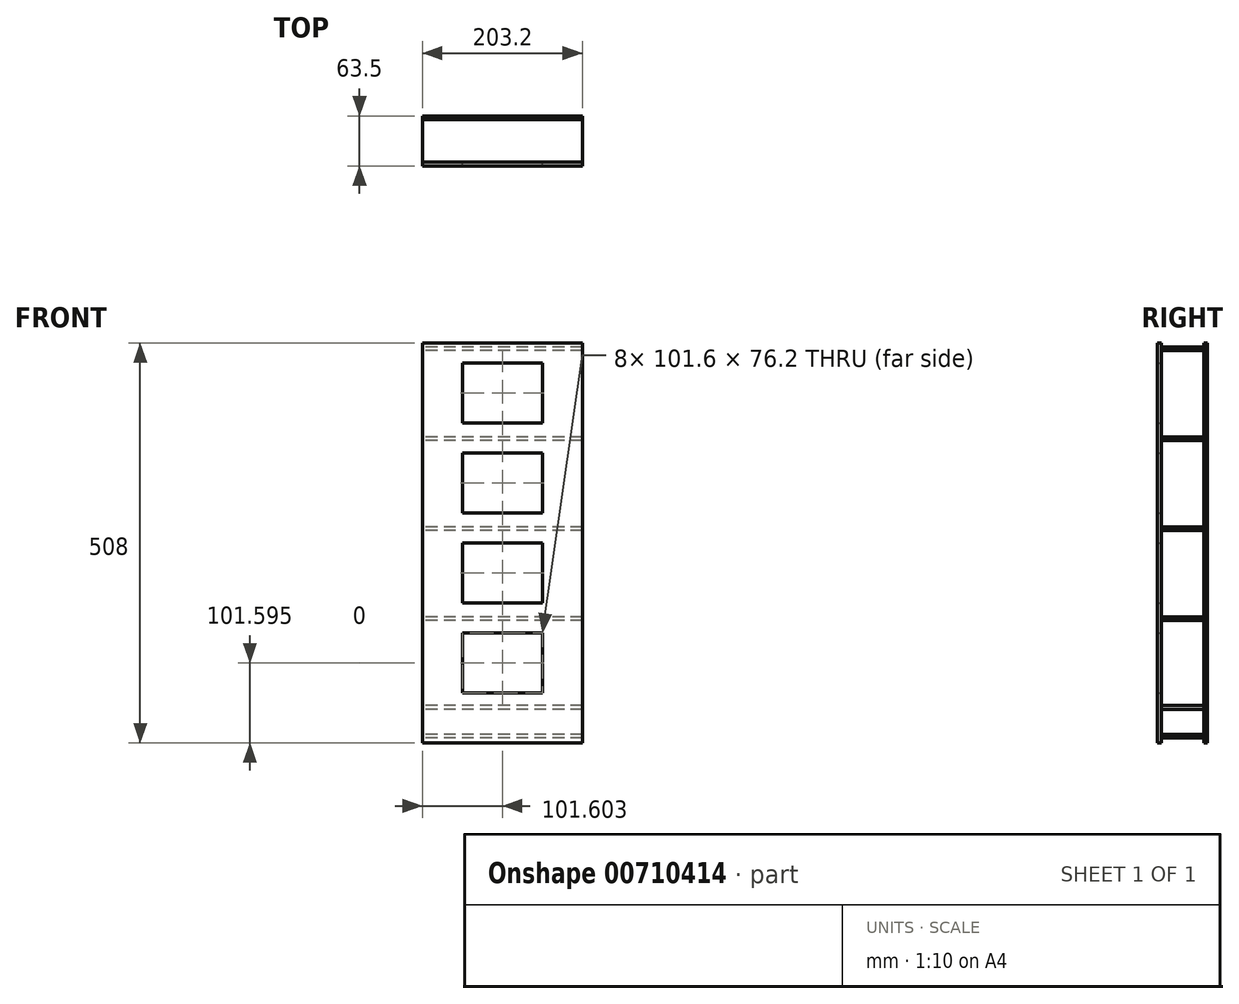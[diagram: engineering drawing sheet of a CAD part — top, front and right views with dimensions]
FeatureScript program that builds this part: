
annotation { "Feature Type Name" : "Feature", "Feature Type Description" : "" }
export const myFeature = defineFeature(function(context is Context, id is Id, definition is map)
    precondition{}
    {
        {
            var Q0;
            Q0=qCreatedBy(makeId("Front.planeOp"),FACE);
            var sketch = newSketch(context, id + "F0", { "sketchPlane" : qUnion([Q0])});
            skLineSegment(sketch, "E0.bottom", {"start": v(-77.18, 365.59) * mm, "end": v(126.02, 365.59) * mm});
            skLineSegment(sketch, "E0.top", {"start": v(-77.18, -142.41) * mm, "end": v(126.02, -142.41) * mm});
            skLineSegment(sketch, "E0.left", {"start": v(-77.18, 365.59) * mm, "end": v(-77.18, -142.41) * mm});
            skLineSegment(sketch, "E0.right", {"start": v(126.02, 365.59) * mm, "end": v(126.02, -142.41) * mm});
            skLineSegment(sketch, "E1.bottom", {"start": v(-26.38, 340.19) * mm, "end": v(75.22, 340.19) * mm});
            skLineSegment(sketch, "E1.top", {"start": v(-26.38, 263.99) * mm, "end": v(75.22, 263.99) * mm});
            skLineSegment(sketch, "E1.left", {"start": v(-26.38, 340.19) * mm, "end": v(-26.38, 263.99) * mm});
            skLineSegment(sketch, "E1.right", {"start": v(75.22, 340.19) * mm, "end": v(75.22, 263.99) * mm});
            skLineSegment(sketch, "E2.bottom", {"start": v(-26.38, 225.89) * mm, "end": v(75.22, 225.89) * mm});
            skLineSegment(sketch, "E2.top", {"start": v(-26.38, 149.69) * mm, "end": v(75.22, 149.69) * mm});
            skLineSegment(sketch, "E2.left", {"start": v(-26.38, 225.89) * mm, "end": v(-26.38, 149.69) * mm});
            skLineSegment(sketch, "E2.right", {"start": v(75.22, 225.89) * mm, "end": v(75.22, 149.69) * mm});
            skLineSegment(sketch, "E3.bottom", {"start": v(-26.38, 111.59) * mm, "end": v(75.22, 111.59) * mm});
            skLineSegment(sketch, "E3.top", {"start": v(-26.38, 35.39) * mm, "end": v(75.22, 35.39) * mm});
            skLineSegment(sketch, "E3.left", {"start": v(-26.38, 111.59) * mm, "end": v(-26.38, 35.39) * mm});
            skLineSegment(sketch, "E3.right", {"start": v(75.22, 111.59) * mm, "end": v(75.22, 35.39) * mm});
            skLineSegment(sketch, "E4.bottom", {"start": v(-26.38, -2.71) * mm, "end": v(75.22, -2.71) * mm});
            skLineSegment(sketch, "E4.top", {"start": v(-26.38, -78.91) * mm, "end": v(75.22, -78.91) * mm});
            skLineSegment(sketch, "E4.left", {"start": v(-26.38, -2.71) * mm, "end": v(-26.38, -78.91) * mm});
            skLineSegment(sketch, "E4.right", {"start": v(75.22, -2.71) * mm, "end": v(75.22, -78.91) * mm});
            skSolve(sketch);
        }
        {
            var Q0;
            Q0=makeQuery(id+"F0.imprint","IMPRINT",FACE,{"disambiguationData":[TD([[makeQuery(id+"F0.imprint","IMPRINT",EDGE,{"derivedFrom":sQuery(id+"F0.wireOp",EDGE,"E0.bottom")}),-1.0]])]});
            extrude(context, id + "F1", {"entities" : qUnion([Q0]), "depth" : 63.5 * mm, "offsetDistance" : 25.4 * mm});
        }
        {
            var Q0;
            Q0=makeQuery(id+"F1.opExtrude","SWEPT_FACE",FACE,{"disambiguationData":[OSD([sQuery(id+"F0.wireOp",EDGE,"E0.right")])]});
            var sketch = newSketch(context, id + "F2", { "sketchPlane" : qUnion([Q0])});
            skLineSegment(sketch, "E5.bottom", {"start": v(-58.74, 365.59) * mm, "end": v(-4.76, 365.59) * mm});
            skLineSegment(sketch, "E5.top", {"start": v(-58.74, -142.41) * mm, "end": v(-4.76, -142.41) * mm});
            skLineSegment(sketch, "E5.left", {"start": v(-58.74, 365.59) * mm, "end": v(-58.74, -142.41) * mm});
            skLineSegment(sketch, "E5.right", {"start": v(-4.76, 365.59) * mm, "end": v(-4.76, -142.41) * mm});
            skSolve(sketch);
        }
        {
            var Q0;
            Q0 = qSketchRegion(id + "F2", true);
            extrude(context, id + "F3", {"entities" : qUnion([Q0]), "operationType" : NewBodyOperationType.REMOVE, "endBound" : BoundingType.THROUGH_ALL, "oppositeDirection" : true, "depth" : 25.4 * mm, "offsetDistance" : 25.4 * mm});
        }
        {
            var Q0;
            Q0=makeQuery(id+"F3.boolean.opBoolean","COPY",FACE,{"derivedFrom":makeQuery(id+"F3.opExtrude","SWEPT_FACE",FACE,{"disambiguationData":[OSD([sQuery(id+"F2.wireOp",EDGE,"E5.left")])]})});
            var sketch = newSketch(context, id + "F4", { "sketchPlane" : qUnion([Q0])});
            skLineSegment(sketch, "E6.bottom", {"start": v(77.18, 360.84) * mm, "end": v(-126.02, 360.84) * mm});
            skLineSegment(sketch, "E6.top", {"start": v(77.18, 356.06) * mm, "end": v(-126.02, 356.06) * mm});
            skLineSegment(sketch, "E6.left", {"start": v(77.18, 360.84) * mm, "end": v(77.18, 356.06) * mm});
            skLineSegment(sketch, "E6.right", {"start": v(-126.02, 360.84) * mm, "end": v(-126.02, 356.06) * mm});
            skLineSegment(sketch, "E7.bottom", {"start": v(77.18, 246.54) * mm, "end": v(-126.02, 246.54) * mm});
            skLineSegment(sketch, "E7.top", {"start": v(77.18, 241.76) * mm, "end": v(-126.02, 241.76) * mm});
            skLineSegment(sketch, "E7.left", {"start": v(77.18, 246.54) * mm, "end": v(77.18, 241.76) * mm});
            skLineSegment(sketch, "E7.right", {"start": v(-126.02, 246.54) * mm, "end": v(-126.02, 241.76) * mm});
            skLineSegment(sketch, "E8.bottom", {"start": v(77.18, 132.24) * mm, "end": v(-126.02, 132.24) * mm});
            skLineSegment(sketch, "E8.top", {"start": v(77.18, 127.46) * mm, "end": v(-126.02, 127.46) * mm});
            skLineSegment(sketch, "E8.left", {"start": v(77.18, 132.24) * mm, "end": v(77.18, 127.46) * mm});
            skLineSegment(sketch, "E8.right", {"start": v(-126.02, 132.24) * mm, "end": v(-126.02, 127.46) * mm});
            skLineSegment(sketch, "E9.bottom", {"start": v(77.18, 17.94) * mm, "end": v(-126.02, 17.94) * mm});
            skLineSegment(sketch, "E9.top", {"start": v(77.18, 13.16) * mm, "end": v(-126.02, 13.16) * mm});
            skLineSegment(sketch, "E9.left", {"start": v(77.18, 17.94) * mm, "end": v(77.18, 13.16) * mm});
            skLineSegment(sketch, "E9.right", {"start": v(-126.02, 17.94) * mm, "end": v(-126.02, 13.16) * mm});
            skLineSegment(sketch, "E10.bottom", {"start": v(77.18, -94.79) * mm, "end": v(-126.02, -94.79) * mm});
            skLineSegment(sketch, "E10.top", {"start": v(77.18, -99.56) * mm, "end": v(-126.02, -99.56) * mm});
            skLineSegment(sketch, "E10.left", {"start": v(77.18, -94.79) * mm, "end": v(77.18, -99.56) * mm});
            skLineSegment(sketch, "E10.right", {"start": v(-126.02, -94.79) * mm, "end": v(-126.02, -99.56) * mm});
            skLineSegment(sketch, "E11.bottom", {"start": v(77.18, -131.29) * mm, "end": v(-126.02, -131.29) * mm});
            skLineSegment(sketch, "E11.top", {"start": v(77.18, -136.06) * mm, "end": v(-126.02, -136.06) * mm});
            skLineSegment(sketch, "E11.left", {"start": v(77.18, -131.29) * mm, "end": v(77.18, -136.06) * mm});
            skLineSegment(sketch, "E11.right", {"start": v(-126.02, -131.29) * mm, "end": v(-126.02, -136.06) * mm});
            skSolve(sketch);
        }
        {
            var Q0;
            Q0 = qSketchRegion(id + "F4", true);
            extrude(context, id + "F5", {"entities" : qUnion([Q0]), "endBound" : BoundingType.UP_TO_NEXT, "depth" : 25.4 * mm, "offsetDistance" : 25.4 * mm});
        }
    });
